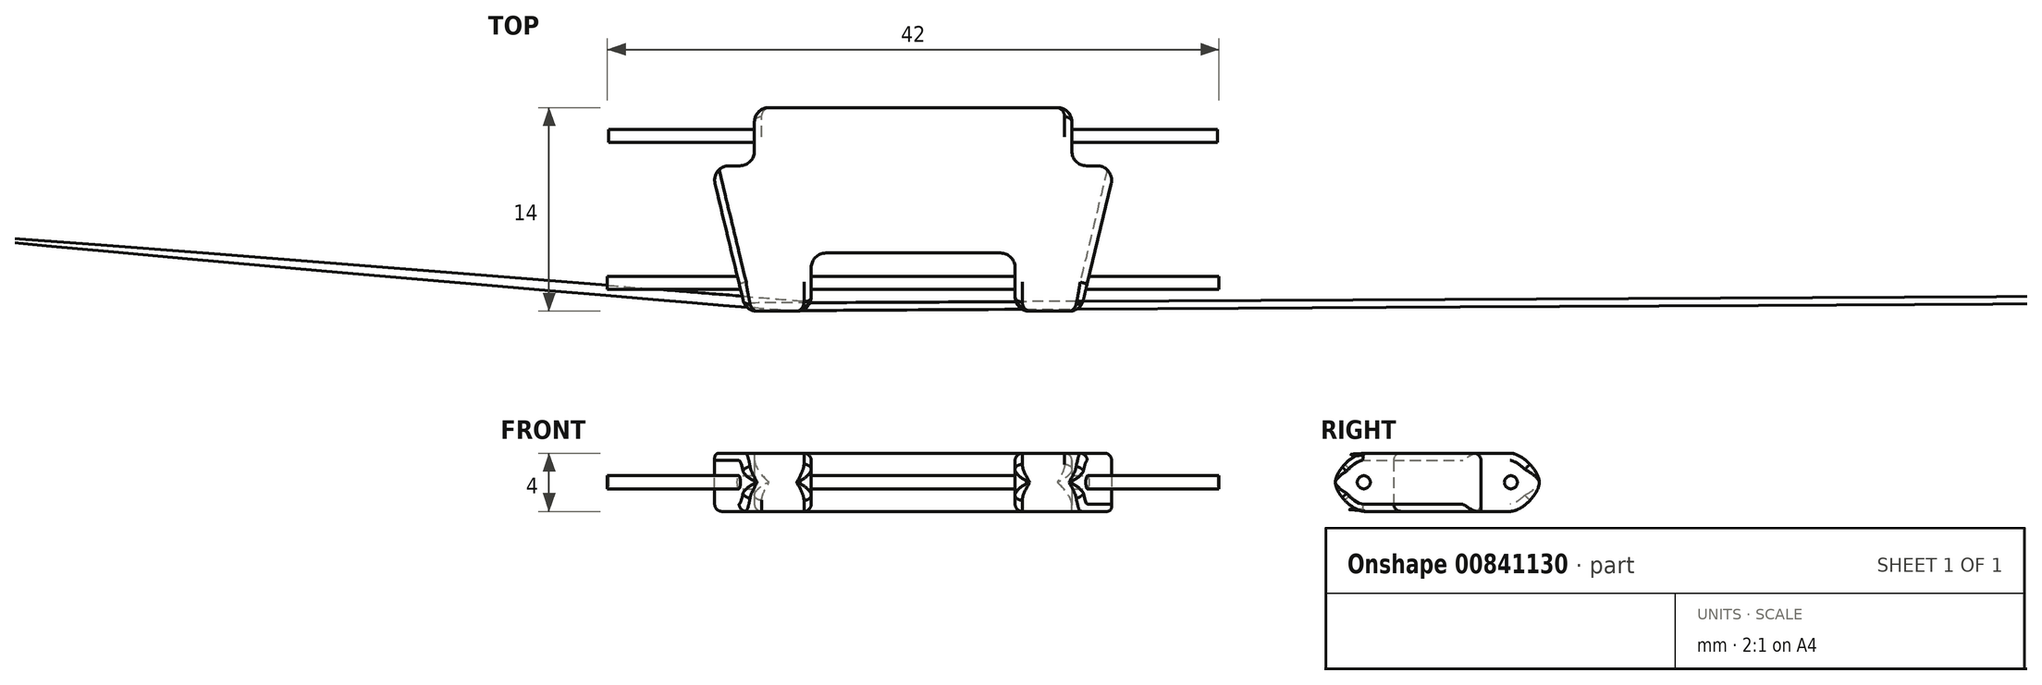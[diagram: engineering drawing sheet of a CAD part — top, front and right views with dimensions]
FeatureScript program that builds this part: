
annotation { "Feature Type Name" : "Feature", "Feature Type Description" : "" }
export const myFeature = defineFeature(function(context is Context, id is Id, definition is map)
    precondition{}
    {
        {
            var Q0;
            Q0=qCreatedBy(makeId("Top.planeOp"),FACE);
            var sketch = newSketch(context, id + "F0", { "sketchPlane" : qUnion([Q0])});
            skLineSegment(sketch, "E0", {"start": v(-14, -4) * mm, "end": v(-11, -4) * mm});
            skLineSegment(sketch, "E1", {"start": v(-11, -4) * mm, "end": v(-11, 0) * mm});
            skLineSegment(sketch, "E2", {"start": v(-11, 0) * mm, "end": v(10.8, 0) * mm});
            skLineSegment(sketch, "E3", {"start": v(-14, -4) * mm, "end": v(-11.6, -14) * mm});
            skLineSegment(sketch, "E4", {"start": v(-11.6, -14) * mm, "end": v(-7.1, -14) * mm});
            skLineSegment(sketch, "E5", {"start": v(-7.1, -14) * mm, "end": v(-7.1, -10) * mm});
            skLineSegment(sketch, "E6", {"start": v(-7.1, -10) * mm, "end": v(6.9, -10) * mm});
            skLineSegment(sketch, "E7", {"start": v(6.9, -10) * mm, "end": v(6.9, -14) * mm});
            skLineSegment(sketch, "E8", {"start": v(6.9, -14) * mm, "end": v(11.4, -14) * mm});
            skLineSegment(sketch, "E9", {"start": v(13.8, -4) * mm, "end": v(10.8, -4) * mm});
            skLineSegment(sketch, "E10", {"start": v(11.4, -14) * mm, "end": v(13.8, -4) * mm});
            skLineSegment(sketch, "E11", {"start": v(10.8, -4) * mm, "end": v(10.8, 0) * mm});
            skSolve(sketch);
        }
        {
            var Q0;
            Q0=makeQuery(id+"F0.imprint","IMPRINT",FACE,{"disambiguationData":[TD([[makeQuery(id+"F0.imprint","IMPRINT",EDGE,{"derivedFrom":sQuery(id+"F0.wireOp",EDGE,"E0")}),-1.0]])]});
            extrude(context, id + "F1", {"entities" : qUnion([Q0]), "depth" : 4 * mm, "offsetDistance" : 25 * mm});
        }
        {
            var Q0;
            Q0=makeQuery(id+"F1.opExtrude","SWEPT_FACE",FACE,{"disambiguationData":[OSD([sQuery(id+"F0.wireOp",EDGE,"E7")])]});
            var sketch = newSketch(context, id + "F2", { "sketchPlane" : qUnion([Q0])});
            skCircle(sketch, "E12", {"center": v(12.05, 2) * mm, "radius": 0.45 * mm});
            skSolve(sketch);
        }
        {
            var Q0;
            Q0=makeQuery(id+"F1.opExtrude","SWEPT_FACE",FACE,{"disambiguationData":[OSD([sQuery(id+"F0.wireOp",EDGE,"E1")])]});
            var sketch = newSketch(context, id + "F3", { "sketchPlane" : qUnion([Q0])});
            skCircle(sketch, "E13", {"center": v(1.95, 2) * mm, "radius": 0.45 * mm});
            skSolve(sketch);
        }
        {
            var Q0;
            Q0=makeQuery(id+"F1.opExtrude","SWEPT_EDGE",EDGE,{"disambiguationData":[OSD([sQuery(id+"F0.wireOp",EDGE,"E5"),sQuery(id+"F0.wireOp",EDGE,"E6")])]});
            var Q1;
            Q1=makeQuery(id+"F1.opExtrude","SWEPT_EDGE",EDGE,{"disambiguationData":[OSD([sQuery(id+"F0.wireOp",EDGE,"E4"),sQuery(id+"F0.wireOp",EDGE,"E5")])]});
            var Q2;
            Q2=makeQuery(id+"F1.opExtrude","SWEPT_EDGE",EDGE,{"disambiguationData":[OSD([sQuery(id+"F0.wireOp",EDGE,"E6"),sQuery(id+"F0.wireOp",EDGE,"E7")])]});
            var Q3;
            Q3=makeQuery(id+"F1.opExtrude","SWEPT_EDGE",EDGE,{"disambiguationData":[OSD([sQuery(id+"F0.wireOp",EDGE,"E7"),sQuery(id+"F0.wireOp",EDGE,"E8")])]});
            var Q4;
            Q4=makeQuery(id+"F1.opExtrude","SWEPT_EDGE",EDGE,{"disambiguationData":[OSD([sQuery(id+"F0.wireOp",EDGE,"E8"),sQuery(id+"F0.wireOp",EDGE,"E10")])]});
            var Q5;
            Q5=makeQuery(id+"F1.opExtrude","SWEPT_EDGE",EDGE,{"disambiguationData":[OSD([sQuery(id+"F0.wireOp",EDGE,"E9"),sQuery(id+"F0.wireOp",EDGE,"E10")])]});
            var Q6;
            Q6=makeQuery(id+"F1.opExtrude","SWEPT_EDGE",EDGE,{"disambiguationData":[OSD([sQuery(id+"F0.wireOp",EDGE,"E9"),sQuery(id+"F0.wireOp",EDGE,"E11")])]});
            var Q7;
            Q7=makeQuery(id+"F1.opExtrude","SWEPT_EDGE",EDGE,{"disambiguationData":[OSD([sQuery(id+"F0.wireOp",EDGE,"E2"),sQuery(id+"F0.wireOp",EDGE,"E11")])]});
            var Q8;
            Q8=makeQuery(id+"F1.opExtrude","SWEPT_EDGE",EDGE,{"disambiguationData":[OSD([sQuery(id+"F0.wireOp",EDGE,"E1"),sQuery(id+"F0.wireOp",EDGE,"E2")])]});
            var Q9;
            Q9=makeQuery(id+"F1.opExtrude","SWEPT_EDGE",EDGE,{"disambiguationData":[OSD([sQuery(id+"F0.wireOp",EDGE,"E0"),sQuery(id+"F0.wireOp",EDGE,"E1")])]});
            var Q10;
            Q10=makeQuery(id+"F1.opExtrude","SWEPT_EDGE",EDGE,{"disambiguationData":[OSD([sQuery(id+"F0.wireOp",EDGE,"E0"),sQuery(id+"F0.wireOp",EDGE,"E3")])]});
            var Q11;
            Q11=makeQuery(id+"F1.opExtrude","SWEPT_EDGE",EDGE,{"disambiguationData":[OSD([sQuery(id+"F0.wireOp",EDGE,"E3"),sQuery(id+"F0.wireOp",EDGE,"E4")])]});
            fillet(context, id + "F4", {"entities" : qUnion([Q0, Q1, Q2, Q3, Q4, Q5, Q6, Q7, Q8, Q9, Q10, Q11]), "radius" : 1 * mm, "tangentPropagation" : true, "allowEdgeOverflow" : false});
        }
        {
            var Q0;
            Q0=makeQuery(id+"F1.opExtrude","CAP_EDGE",EDGE,{"disambiguationData":[OSD([sQuery(id+"F0.wireOp",EDGE,"E4")])],"isStart":false});
            var Q1;
            Q1=makeQuery(id+"F1.opExtrude","CAP_EDGE",EDGE,{"disambiguationData":[OSD([sQuery(id+"F0.wireOp",EDGE,"E4")])],"isStart":true});
            var Q2;
            Q2=makeQuery(id+"F1.opExtrude","CAP_EDGE",EDGE,{"disambiguationData":[OSD([sQuery(id+"F0.wireOp",EDGE,"E8")])],"isStart":false});
            var Q3;
            Q3=makeQuery(id+"F1.opExtrude","CAP_EDGE",EDGE,{"disambiguationData":[OSD([sQuery(id+"F0.wireOp",EDGE,"E8")])],"isStart":true});
            var Q4;
            Q4=makeQuery(id+"F1.opExtrude","CAP_EDGE",EDGE,{"disambiguationData":[OSD([sQuery(id+"F0.wireOp",EDGE,"E2")])],"isStart":false});
            var Q5;
            Q5=makeQuery(id+"F1.opExtrude","CAP_EDGE",EDGE,{"disambiguationData":[OSD([sQuery(id+"F0.wireOp",EDGE,"E2")])],"isStart":true});
            fillet(context, id + "F5", {"entities" : qUnion([Q0, Q1, Q2, Q3, Q4, Q5]), "radius" : 2 * mm, "rho" : 0.3, "crossSection" : FilletCrossSection.CONIC, "allowEdgeOverflow" : false});
        }
        {
            var Q0;
            Q0=makeQuery(id+"F5.opFillet","BLEND_EDGE",EDGE,{"blendedFrom":[makeQuery(id+"F1.opExtrude","CAP_EDGE",EDGE,{"disambiguationData":[OSD([sQuery(id+"F0.wireOp",EDGE,"E4")])],"isStart":false}),makeQuery(id+"F1.opExtrude","SWEPT_FACE",FACE,{"disambiguationData":[OSD([sQuery(id+"F0.wireOp",EDGE,"E5")])]})],"blendedInto":[makeQuery(id+"F1.opExtrude","SWEPT_FACE",FACE,{"disambiguationData":[OSD([sQuery(id+"F0.wireOp",EDGE,"E5")])]})]});
            var Q1;
            Q1=makeQuery(id+"F1.opExtrude","CAP_EDGE",EDGE,{"disambiguationData":[OSD([sQuery(id+"F0.wireOp",EDGE,"E5")])],"isStart":false});
            var Q2;
            {var subQ0=sQuery(id+"F0.wireOp",EDGE,"E6");var subQ1=sQuery(id+"F0.wireOp",EDGE,"E5");Q2=makeQuery(id+"F4.opFillet","BLEND_EDGE",EDGE,{"blendedFrom":[makeQuery(id+"F1.opExtrude","SWEPT_EDGE",EDGE,{"disambiguationData":[OSD([subQ1,subQ0])]}),makeQuery(id+"F1.opExtrude","CAP_FACE",FACE,{"disambiguationData":[OSD([sQuery(id+"F0.wireOp",EDGE,"E0"),sQuery(id+"F0.wireOp",EDGE,"E1"),sQuery(id+"F0.wireOp",EDGE,"E2"),sQuery(id+"F0.wireOp",EDGE,"E3"),sQuery(id+"F0.wireOp",EDGE,"E4"),subQ1,subQ0,sQuery(id+"F0.wireOp",EDGE,"E7"),sQuery(id+"F0.wireOp",EDGE,"E8"),sQuery(id+"F0.wireOp",EDGE,"E9"),sQuery(id+"F0.wireOp",EDGE,"E10"),sQuery(id+"F0.wireOp",EDGE,"E11")])],"isStart":false})],"blendedInto":[makeQuery(id+"F1.opExtrude","CAP_FACE",FACE,{"disambiguationData":[OSD([sQuery(id+"F0.wireOp",EDGE,"E0"),sQuery(id+"F0.wireOp",EDGE,"E1"),sQuery(id+"F0.wireOp",EDGE,"E2"),sQuery(id+"F0.wireOp",EDGE,"E3"),sQuery(id+"F0.wireOp",EDGE,"E4"),subQ1,subQ0,sQuery(id+"F0.wireOp",EDGE,"E7"),sQuery(id+"F0.wireOp",EDGE,"E8"),sQuery(id+"F0.wireOp",EDGE,"E9"),sQuery(id+"F0.wireOp",EDGE,"E10"),sQuery(id+"F0.wireOp",EDGE,"E11")])],"isStart":false})]});}
            var Q3;
            {var subQ0=sQuery(id+"F0.wireOp",EDGE,"E8");Q3=makeQuery(id+"F5.opFillet","BLEND_EDGE",EDGE,{"blendedFrom":[makeQuery(id+"F1.opExtrude","CAP_EDGE",EDGE,{"disambiguationData":[OSD([subQ0])],"isStart":true}),makeQuery(id+"F4.opFillet","BLEND_FACE",FACE,{"disambiguationData":[OSD([sQuery(id+"F0.wireOp",EDGE,"E7"),subQ0])]})],"blendedInto":[makeQuery(id+"F4.opFillet","BLEND_FACE",FACE,{"disambiguationData":[OSD([sQuery(id+"F0.wireOp",EDGE,"E7"),subQ0])]})]});}
            var Q4;
            {var subQ0=sQuery(id+"F0.wireOp",EDGE,"E4");Q4=makeQuery(id+"F5.opFillet","BLEND_EDGE",EDGE,{"blendedFrom":[makeQuery(id+"F1.opExtrude","CAP_EDGE",EDGE,{"disambiguationData":[OSD([subQ0])],"isStart":false}),makeQuery(id+"F4.opFillet","BLEND_FACE",FACE,{"disambiguationData":[OSD([sQuery(id+"F0.wireOp",EDGE,"E3"),subQ0])]})],"blendedInto":[makeQuery(id+"F4.opFillet","BLEND_FACE",FACE,{"disambiguationData":[OSD([sQuery(id+"F0.wireOp",EDGE,"E3"),subQ0])]})]});}
            var Q5;
            {var subQ0=sQuery(id+"F0.wireOp",EDGE,"E4");Q5=makeQuery(id+"F5.opFillet","BLEND_EDGE",EDGE,{"blendedFrom":[makeQuery(id+"F1.opExtrude","CAP_EDGE",EDGE,{"disambiguationData":[OSD([subQ0])],"isStart":true}),makeQuery(id+"F4.opFillet","BLEND_FACE",FACE,{"disambiguationData":[OSD([sQuery(id+"F0.wireOp",EDGE,"E3"),subQ0])]})],"blendedInto":[makeQuery(id+"F4.opFillet","BLEND_FACE",FACE,{"disambiguationData":[OSD([sQuery(id+"F0.wireOp",EDGE,"E3"),subQ0])]})]});}
            var Q6;
            Q6=makeQuery(id+"F5.opFillet","BLEND_EDGE",EDGE,{"blendedFrom":[makeQuery(id+"F1.opExtrude","CAP_EDGE",EDGE,{"disambiguationData":[OSD([sQuery(id+"F0.wireOp",EDGE,"E8")])],"isStart":false}),makeQuery(id+"F1.opExtrude","SWEPT_FACE",FACE,{"disambiguationData":[OSD([sQuery(id+"F0.wireOp",EDGE,"E10")])]})],"blendedInto":[makeQuery(id+"F1.opExtrude","SWEPT_FACE",FACE,{"disambiguationData":[OSD([sQuery(id+"F0.wireOp",EDGE,"E10")])]})]});
            var Q7;
            {var subQ0=sQuery(id+"F0.wireOp",EDGE,"E8");Q7=makeQuery(id+"F5.opFillet","BLEND_EDGE",EDGE,{"blendedFrom":[makeQuery(id+"F1.opExtrude","CAP_EDGE",EDGE,{"disambiguationData":[OSD([subQ0])],"isStart":true}),makeQuery(id+"F4.opFillet","BLEND_FACE",FACE,{"disambiguationData":[OSD([subQ0,sQuery(id+"F0.wireOp",EDGE,"E10")])]})],"blendedInto":[makeQuery(id+"F4.opFillet","BLEND_FACE",FACE,{"disambiguationData":[OSD([subQ0,sQuery(id+"F0.wireOp",EDGE,"E10")])]})]});}
            fillet(context, id + "F6", {"entities" : qUnion([Q0, Q1, Q2, Q3, Q4, Q5, Q6, Q7]), "radius" : 0.5 * mm, "tangentPropagation" : true, "allowEdgeOverflow" : false});
        }
        {
            var Q0;
            Q0=makeQuery(id+"F3.imprint","IMPRINT",FACE,{"disambiguationData":[TD([[makeQuery(id+"F3.imprint","IMPRINT",EDGE,{"derivedFrom":sQuery(id+"F3.wireOp",EDGE,"E13")}),1.0]])]});
            extrude(context, id + "F7", {"entities" : qUnion([Q0]), "operationType" : NewBodyOperationType.ADD, "depth" : 10 * mm, "offsetDistance" : 25 * mm, "hasSecondDirection" : true, "secondDirectionOppositeDirection" : true, "secondDirectionDepth" : 31.8 * mm});
        }
        {
            var Q0;
            Q0=makeQuery(id+"F2.imprint","IMPRINT",FACE,{"disambiguationData":[TD([[makeQuery(id+"F2.imprint","IMPRINT",EDGE,{"derivedFrom":sQuery(id+"F2.wireOp",EDGE,"E12")}),1.0]])]});
            extrude(context, id + "F8", {"entities" : qUnion([Q0]), "operationType" : NewBodyOperationType.ADD, "depth" : 28 * mm, "offsetDistance" : 25 * mm, "hasSecondDirection" : true, "secondDirectionOppositeDirection" : true, "secondDirectionDepth" : 14 * mm});
        }
    });
